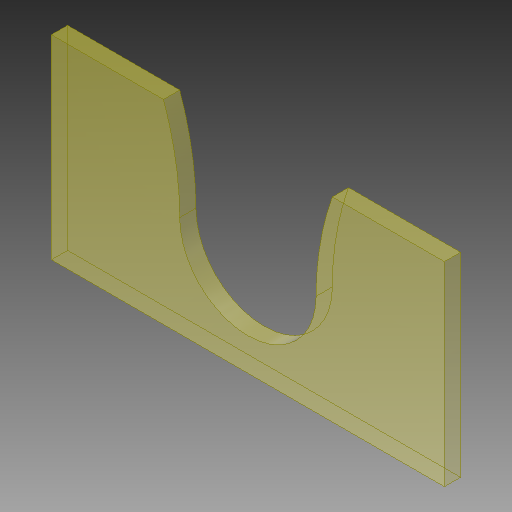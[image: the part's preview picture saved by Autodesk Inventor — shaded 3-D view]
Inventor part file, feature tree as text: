
AUTODESK INVENTOR PART (.ipt)
format: ipt  version: 2018.1 (Build 221171000, 171)  size: 125,952 bytes
history: native  units: mm
features: other x5, extrude x3, sketch x3, reference x1
ambient origin geometry x8: Origin, YZ Plane, XZ Plane, XY Plane, X Axis, Y Axis, Z Axis, Center Point
bodies: Solid1 (feature_tree)
feature tree (12):
  parser-record x2  (decoder bookkeeping rows leaked as tree rows — omitted from the tree; the rows remain in map.json)
  extrude  "Extrusion1"  Depth=60.0mm
  extrude  "Extrusion2"  TaperAngle=0.0deg  [1 undecoded]
  extrude  "Extrusion5"  Depth=5.0mm
  sketch  "Sketch1"  dims[d0=121.0mm d1=60.0mm]
  sketch  "Sketch2"  dims[d2=5.0mm d3=0.0mm]
  sketch  "Sketch4"  dims[d4=5.0mm d5=0.0mm d28=26.0mm d30=21.0mm d33=32.0mm d34=180.0deg d35=90.0deg d36=26.0mm d37=5.0mm d38=0.0mm d39=0.0mm]
  reference  "Reference3"
  other  "full_assembly.iam"
  other  "tank_assembly:1"
  other  "tank_back:1"
note: 1 required parameter value undecoded (feature->parameter linkage not recoverable at this tier; creation-order binding heuristic only, values carry confidence <= 0.55)
note: 2 file-system paths scrubbed to <path> (originals preserved in map.json)
